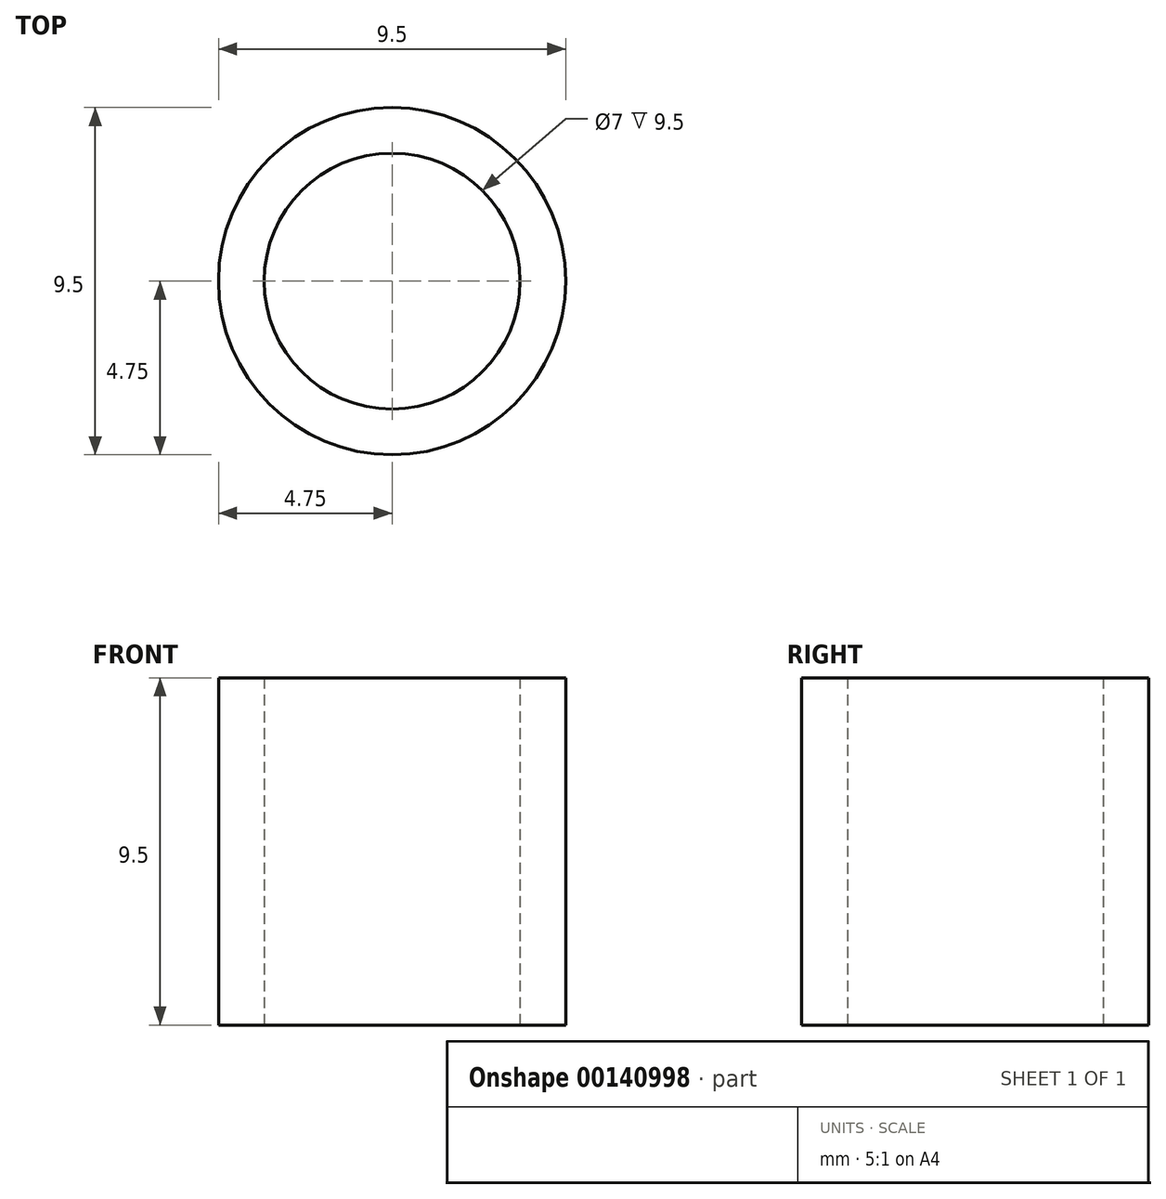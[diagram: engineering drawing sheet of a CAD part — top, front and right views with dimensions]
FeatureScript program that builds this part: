
annotation { "Feature Type Name" : "Feature", "Feature Type Description" : "" }
export const myFeature = defineFeature(function(context is Context, id is Id, definition is map)
    precondition{}
    {
        {
            var Q0;
            Q0=qCreatedBy(makeId("Top.planeOp"),FACE);
            var sketch = newSketch(context, id + "F0", { "sketchPlane" : qUnion([Q0])});
            skCircle(sketch, "E0", {"center": v(0, 0) * mm, "radius": 3.5 * mm});
            skCircle(sketch, "E1", {"center": v(0, 0) * mm, "radius": 4.75 * mm});
            skSolve(sketch);
        }
        {
            var Q0;
            Q0=makeQuery(id+"F0.imprint","IMPRINT",FACE,{"disambiguationData":[TD([[makeQuery(id+"F0.imprint","IMPRINT",EDGE,{"derivedFrom":sQuery(id+"F0.wireOp",EDGE,"E0")}),-1.0]])]});
            extrude(context, id + "F1", {"entities" : qUnion([Q0]), "depth" : 9.5 * mm});
        }
    });
